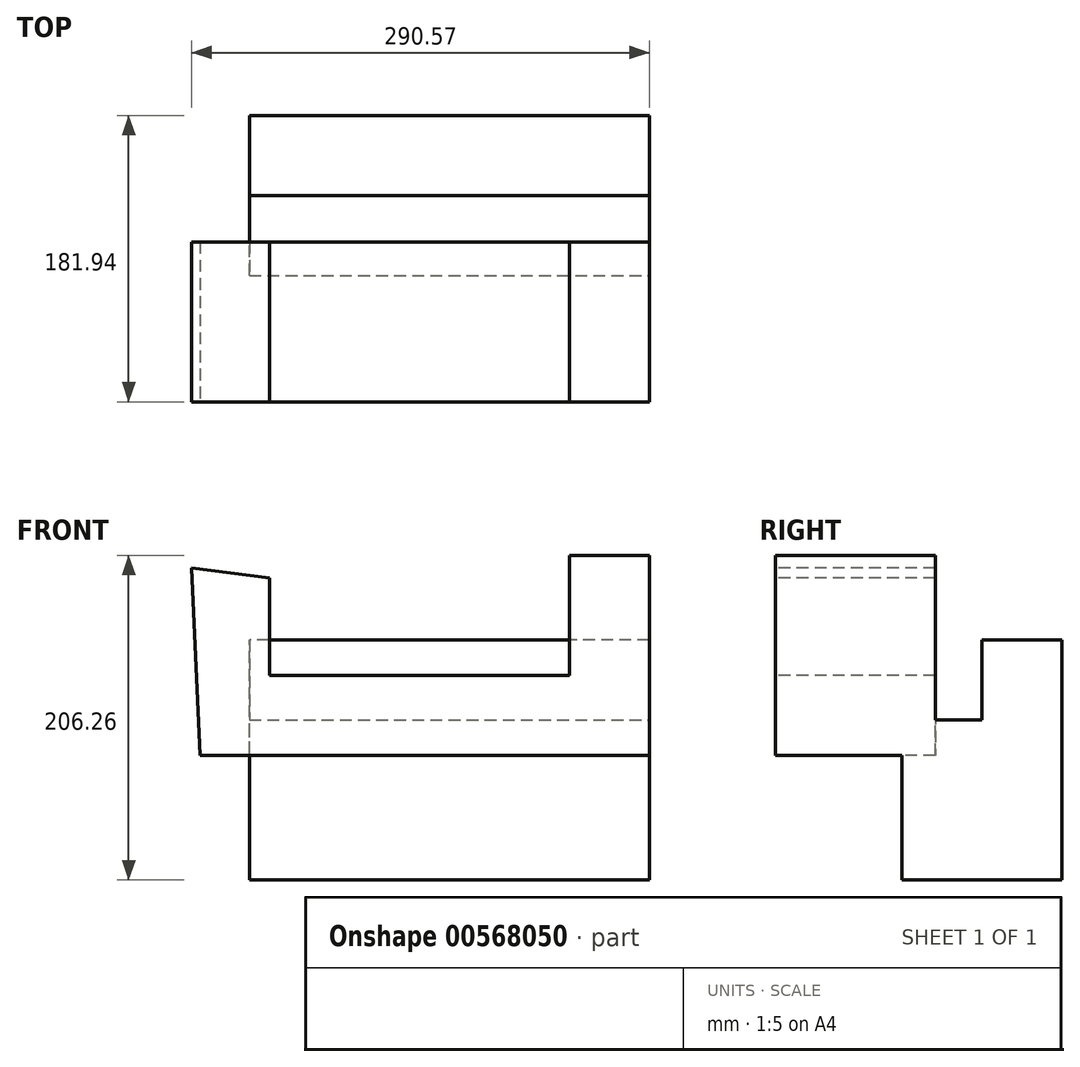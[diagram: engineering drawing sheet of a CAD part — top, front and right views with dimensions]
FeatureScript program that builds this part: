
annotation { "Feature Type Name" : "Feature", "Feature Type Description" : "" }
export const myFeature = defineFeature(function(context is Context, id is Id, definition is map)
    precondition{}
    {
        {
            var Q0;
            Q0=qCreatedBy(makeId("Front.planeOp"),FACE);
            var sketch = newSketch(context, id + "F0", { "sketchPlane" : qUnion([Q0])});
            skLineSegment(sketch, "E0", {"start": v(0, 0) * mm, "end": v(254, 0) * mm});
            skLineSegment(sketch, "E1", {"start": v(254, 0) * mm, "end": v(254, 127) * mm});
            skLineSegment(sketch, "E2", {"start": v(254, 127) * mm, "end": v(203.2, 127) * mm});
            skLineSegment(sketch, "E3", {"start": v(203.2, 127) * mm, "end": v(203.2, 50.8) * mm});
            skLineSegment(sketch, "E4", {"start": v(203.2, 50.8) * mm, "end": v(12.7, 50.8) * mm});
            skLineSegment(sketch, "E5", {"start": v(12.7, 50.8) * mm, "end": v(12.7, 112.53) * mm});
            skLineSegment(sketch, "E6", {"start": v(12.7, 112.53) * mm, "end": v(-36.57, 119.04) * mm});
            skLineSegment(sketch, "E7", {"start": v(-36.57, 119.04) * mm, "end": v(-31.36, 0) * mm});
            skLineSegment(sketch, "E8", {"start": v(-31.36, 0) * mm, "end": v(0, 0) * mm});
            skSolve(sketch);
        }
        {
            var Q0;
            Q0=makeQuery(id+"F0.imprint","IMPRINT",FACE,{"disambiguationData":[TD([[makeQuery(id+"F0.imprint","IMPRINT",EDGE,{"derivedFrom":sQuery(id+"F0.wireOp",EDGE,"E0")}),1.0]])]});
            extrude(context, id + "F1", {"entities" : qUnion([Q0]), "oppositeDirection" : true, "depth" : 101.6 * mm, "offsetDistance" : 25.4 * mm});
        }
        {
            var Q0;
            Q0=qCreatedBy(makeId("Right.planeOp"),FACE);
            var sketch = newSketch(context, id + "F2", { "sketchPlane" : qUnion([Q0])});
            skLineSegment(sketch, "E9", {"start": v(80.34, -79.26) * mm, "end": v(181.94, -79.26) * mm});
            skLineSegment(sketch, "E10", {"start": v(181.94, -79.26) * mm, "end": v(181.94, 73.14) * mm});
            skLineSegment(sketch, "E11", {"start": v(181.94, 73.14) * mm, "end": v(131.14, 73.14) * mm});
            skLineSegment(sketch, "E12", {"start": v(131.14, 73.14) * mm, "end": v(131.14, 22.34) * mm});
            skLineSegment(sketch, "E13", {"start": v(131.14, 22.34) * mm, "end": v(80.34, 22.34) * mm});
            skLineSegment(sketch, "E14", {"start": v(80.34, 22.34) * mm, "end": v(80.34, -79.26) * mm});
            skSolve(sketch);
        }
        {
            var Q0;
            Q0=makeQuery(id+"F2.imprint","IMPRINT",FACE,{"disambiguationData":[TD([[makeQuery(id+"F2.imprint","IMPRINT",EDGE,{"derivedFrom":sQuery(id+"F2.wireOp",EDGE,"E9")}),1.0]])]});
            extrude(context, id + "F3", {"entities" : qUnion([Q0]), "operationType" : NewBodyOperationType.ADD, "depth" : 254 * mm, "offsetDistance" : 25.4 * mm});
        }
    });
